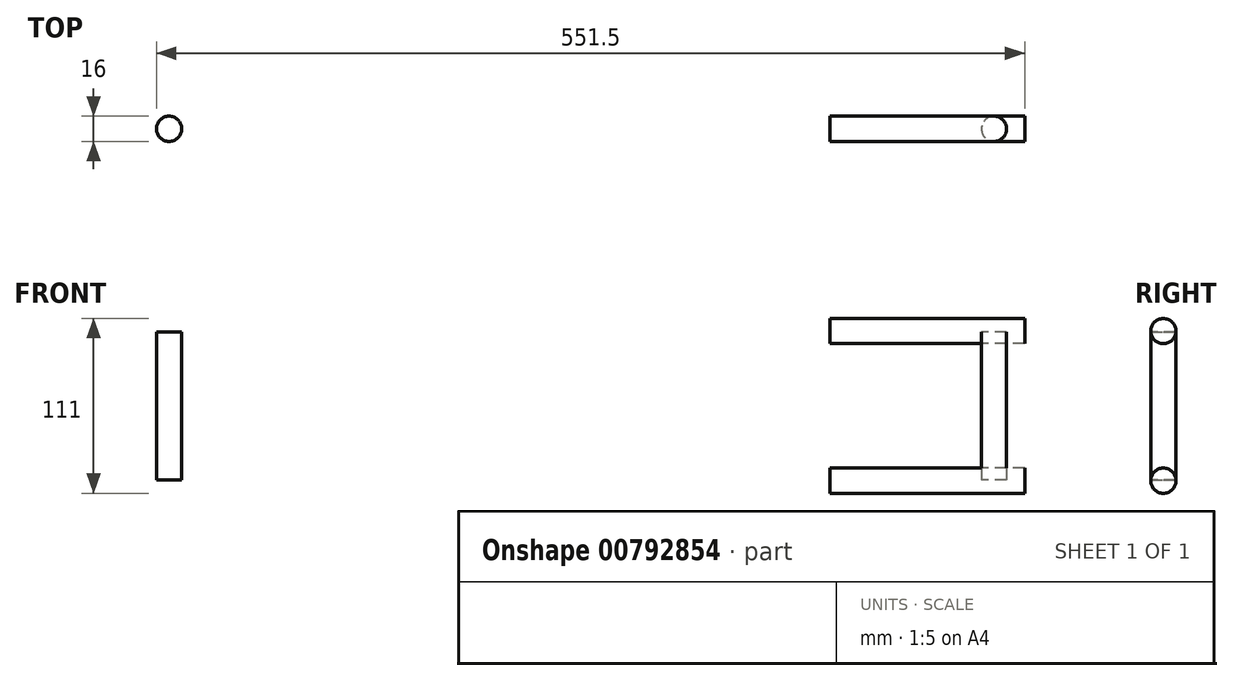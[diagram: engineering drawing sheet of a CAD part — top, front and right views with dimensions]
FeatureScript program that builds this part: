
annotation { "Feature Type Name" : "Feature", "Feature Type Description" : "" }
export const myFeature = defineFeature(function(context is Context, id is Id, definition is map)
    precondition{}
    {
        {
            var Q0;
            Q0=qCreatedBy(makeId("Right.planeOp"),FACE);
            var sketch = newSketch(context, id + "F0", { "sketchPlane" : qUnion([Q0])});
            skLineSegment(sketch, "E0", {"start": v(-41.18, 0) * mm, "end": v(48.96, 0) * mm, "construction": true});
            skLineSegment(sketch, "E1", {"start": v(0, 63.71) * mm, "end": v(0, -62.07) * mm, "construction": true});
            skCircle(sketch, "E2", {"center": v(0, 47.5) * mm, "radius": 8 * mm});
            skCircle(sketch, "E3", {"center": v(0, -47.5) * mm, "radius": 8 * mm});
            skSolve(sketch);
        }
        {
            var Q0;
            Q0 = qSketchRegion(id + "F0", true);
            extrude(context, id + "F1", {"entities" : qUnion([Q0]), "depth" : 563 * mm, "offsetDistance" : 25 * mm});
        }
        {
            var Q0;
            Q0=qCreatedBy(makeId("Front.planeOp"),FACE);
            var sketch = newSketch(context, id + "F2", { "sketchPlane" : qUnion([Q0])});
            skLineSegment(sketch, "E4", {"start": v(597.28, 72.97) * mm, "end": v(597.28, -69.74) * mm});
            skLineSegment(sketch, "E5", {"start": v(439.28, -69.74) * mm, "end": v(439.28, 72.97) * mm});
            skLineSegment(sketch, "E6", {"start": v(281.28, 72.97) * mm, "end": v(281.28, -69.74) * mm});
            skLineSegment(sketch, "E7", {"start": v(123.28, -69.74) * mm, "end": v(123.28, 72.97) * mm});
            skLineSegment(sketch, "E8", {"start": v(-34.72, 72.97) * mm, "end": v(-34.72, -69.74) * mm});
            skLineSegment(sketch, "E9", {"start": v(-34.72, -69.74) * mm, "end": v(123.28, -69.74) * mm});
            skLineSegment(sketch, "E10", {"start": v(123.28, -69.74) * mm, "end": v(281.28, -69.74) * mm});
            skLineSegment(sketch, "E11", {"start": v(281.28, -69.74) * mm, "end": v(439.28, -69.74) * mm});
            skLineSegment(sketch, "E12", {"start": v(439.28, -69.74) * mm, "end": v(597.28, -69.74) * mm});
            skLineSegment(sketch, "E13", {"start": v(439.28, 72.97) * mm, "end": v(281.28, 72.97) * mm});
            skLineSegment(sketch, "E14", {"start": v(281.28, 72.97) * mm, "end": v(123.28, 72.97) * mm});
            skLineSegment(sketch, "E15", {"start": v(123.28, 72.97) * mm, "end": v(-34.72, 72.97) * mm});
            skSolve(sketch);
        }
        {
            var Q0;
            Q0 = qSketchRegion(id + "F2", true);
            extrude(context, id + "F3", {"entities" : qUnion([Q0]), "operationType" : NewBodyOperationType.REMOVE, "depth" : 25 * mm, "offsetDistance" : 25 * mm, "hasSecondDirection" : true, "secondDirectionOppositeDirection" : true, "secondDirectionDepth" : 25 * mm});
        }
        {
            var Q0;
            Q0=qCreatedBy(makeId("Top.planeOp"),FACE);
            var sketch = newSketch(context, id + "F4", { "sketchPlane" : qUnion([Q0])});
            skLineSegment(sketch, "E16", {"start": v(-21.1, 0) * mm, "end": v(692.91, 0) * mm, "construction": true});
            skCircle(sketch, "E17", {"center": v(19.5, 0) * mm, "radius": 8 * mm});
            skLineSegment(sketch, "E18", {"start": v(0, 30.75) * mm, "end": v(0, -22.71) * mm, "construction": true});
            skLineSegment(sketch, "E19", {"start": v(281.5, -251.99) * mm, "end": v(281.5, 273.38) * mm, "construction": true});
            skCircle(sketch, "E20.MirrorC", {"center": v(543.5, 0) * mm, "radius": 8 * mm});
            skLineSegment(sketch, "E21", {"start": v(402.75, 273.38) * mm, "end": v(402.75, -251.99) * mm, "construction": true});
            skLineSegment(sketch, "E22", {"start": v(160.25, 273.38) * mm, "end": v(160.25, -251.99) * mm, "construction": true});
            skSolve(sketch);
        }
        {
            var Q0;
            Q0 = qSketchRegion(id + "F4", true);
            extrude(context, id + "F5", {"entities" : qUnion([Q0]), "depth" : 47 * mm, "offsetDistance" : 25 * mm, "hasSecondDirection" : true, "secondDirectionOppositeDirection" : true, "secondDirectionDepth" : 47 * mm});
        }
    });
